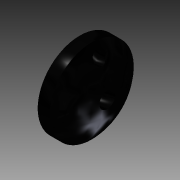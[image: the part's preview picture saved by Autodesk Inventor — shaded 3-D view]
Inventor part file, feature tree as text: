
AUTODESK INVENTOR PART (.ipt)
format: ipt  version: 2014 (Build 180170000, 170)  size: 134,144 bytes
history: native  units: in
note: dims shown in document units (in); Inventor stores cm internally (conversion verified against a paired STEP export)
features: sketch x4, plane x3, extrude x3, revolve x1, chamfer x1, reference x1
ambient origin geometry x8: Origin, YZ Plane, XZ Plane, XY Plane, X Axis, Y Axis, Z Axis, Center Point
bodies: Solid1 (feature_tree)
feature tree (13):
  revolve  "Revolution1"  [1 undecoded]
  plane  "Work Plane3"
  extrude  "Extrusion3"  Depth=0.127in
  extrude  "Extrusion4"  Depth=0.273in
  plane  "Work Plane4"
  extrude  "Extrusion5"  TaperAngle=90.0deg  [1 undecoded]
  chamfer  "Chamfer1"  [1 undecoded]
  sketch  "Sketch1"  dims[d0=0.08in d1=0.532in]
  plane  "Work Plane2"
  sketch  "Sketch4"  dims[d2=0.24in d3=0.127in]
  reference  "Reference1"
  sketch  "Sketch5"  dims[d4=0.15in d5=0.273in]
  sketch  "Sketch6"  dims[d7=0.2in d8=90.0deg d9=-0.05in d16=0.26in d17=0.0in d18=0.09in d19=1.0in d20=0.0in d21=-0.125in d22=0.2in d23=1.0in d24=0.0in d25=0.05in d26=0.125in d27=45.0deg]
note: 3 required parameter values undecoded (feature->parameter linkage not recoverable at this tier; creation-order binding heuristic only, values carry confidence <= 0.55)